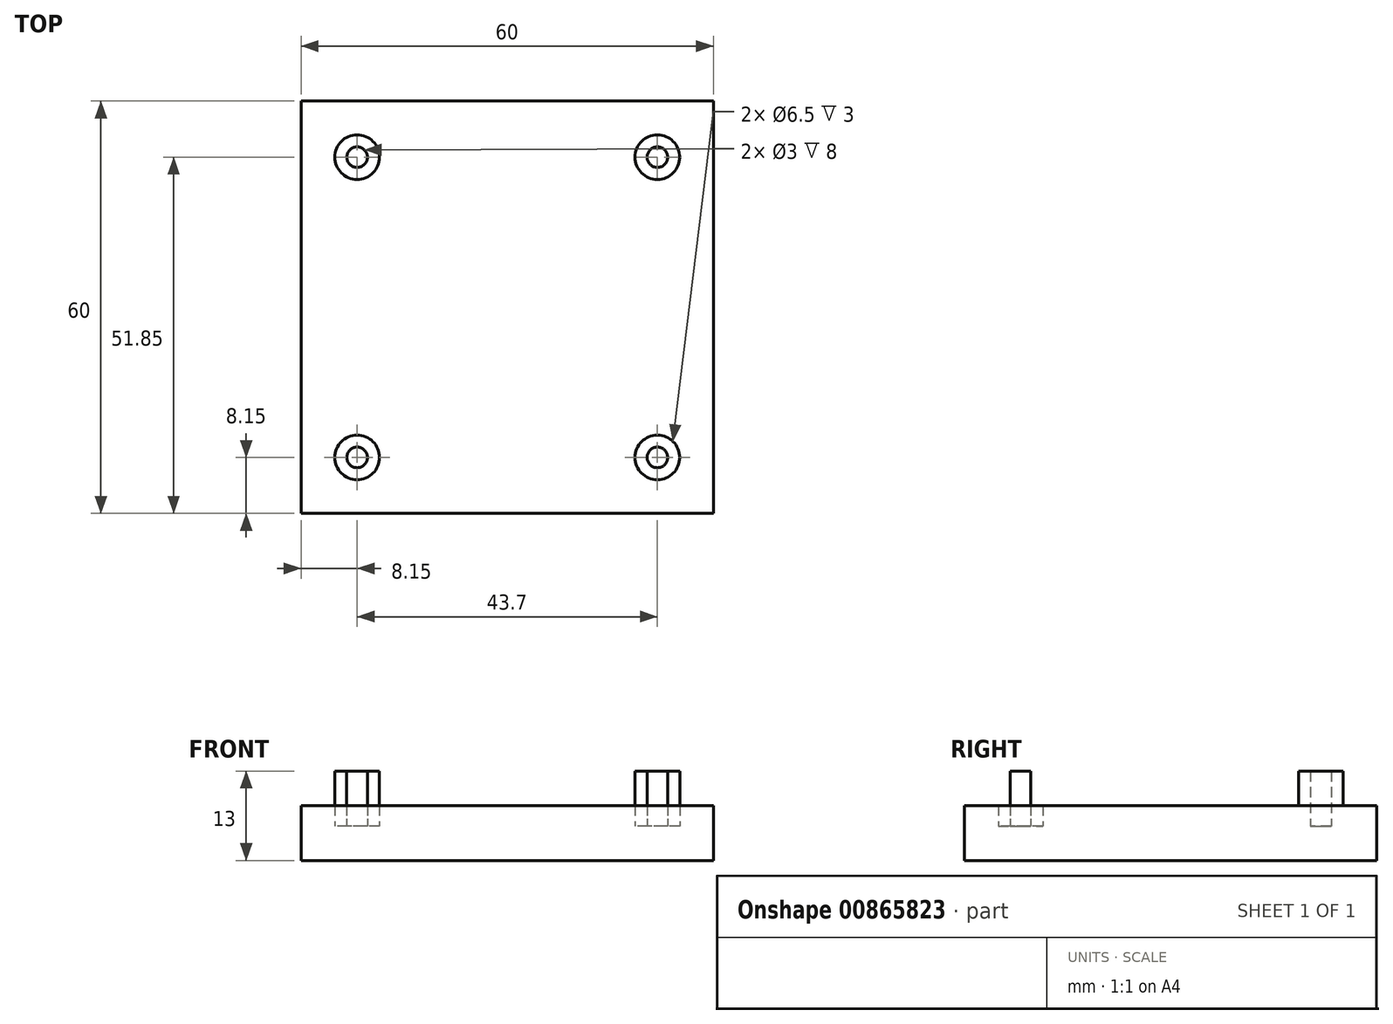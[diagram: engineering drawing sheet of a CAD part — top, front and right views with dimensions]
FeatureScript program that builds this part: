
annotation { "Feature Type Name" : "Feature", "Feature Type Description" : "" }
export const myFeature = defineFeature(function(context is Context, id is Id, definition is map)
    precondition{}
    {
        {
            var Q0;
            Q0=qCreatedBy(makeId("Top.planeOp"),FACE);
            var sketch = newSketch(context, id + "F0", { "sketchPlane" : qUnion([Q0])});
            skLineSegment(sketch, "E0.bottom", {"start": v(30, -40) * mm, "end": v(-30, -40) * mm});
            skLineSegment(sketch, "E0.top", {"start": v(30, 40) * mm, "end": v(-30, 40) * mm});
            skLineSegment(sketch, "E0.left", {"start": v(30, -40) * mm, "end": v(30, 40) * mm});
            skLineSegment(sketch, "E0.right", {"start": v(-30, -40) * mm, "end": v(-30, 40) * mm});
            skPoint(sketch, "E0.middle", {"position": v(0, 0) * mm});
            skLineSegment(sketch, "E1.bottom", {"start": v(30, -30) * mm, "end": v(-30, -30) * mm});
            skLineSegment(sketch, "E1.top", {"start": v(30, 30) * mm, "end": v(-30, 30) * mm});
            skLineSegment(sketch, "E1.left", {"start": v(30, -30) * mm, "end": v(30, 30) * mm});
            skLineSegment(sketch, "E1.right", {"start": v(-30, -30) * mm, "end": v(-30, 30) * mm});
            skCircle(sketch, "E2", {"center": v(-15, 35) * mm, "radius": 1.7 * mm});
            skCircle(sketch, "E3", {"center": v(15, 35) * mm, "radius": 1.7 * mm});
            skCircle(sketch, "E4.MirrorC", {"center": v(15, -35) * mm, "radius": 1.7 * mm});
            skCircle(sketch, "E5.MirrorC", {"center": v(-15, -35) * mm, "radius": 1.7 * mm});
            skCircle(sketch, "E6", {"center": v(-21.85, 21.85) * mm, "radius": 1.5 * mm});
            skCircle(sketch, "E7", {"center": v(21.85, 21.85) * mm, "radius": 1.5 * mm});
            skCircle(sketch, "E8.MirrorC", {"center": v(-21.85, -21.85) * mm, "radius": 1.5 * mm});
            skCircle(sketch, "E9.MirrorC", {"center": v(21.85, -21.85) * mm, "radius": 1.5 * mm});
            skCircle(sketch, "E10", {"center": v(-21.85, 21.85) * mm, "radius": 3.25 * mm});
            skCircle(sketch, "E11", {"center": v(21.85, 21.85) * mm, "radius": 3.25 * mm});
            skCircle(sketch, "E12.MirrorC", {"center": v(21.85, -21.85) * mm, "radius": 3.25 * mm});
            skCircle(sketch, "E13.MirrorC", {"center": v(-21.85, -21.85) * mm, "radius": 3.25 * mm});
            skSolve(sketch);
        }
        {
            var Q0;
            Q0=makeQuery(id+"F0.imprint","IMPRINT",FACE,{"disambiguationData":[TD([[makeQuery(id+"F0.imprint","IMPRINT",EDGE,{"derivedFrom":sQuery(id+"F0.wireOp",EDGE,"E1.bottom")}),-1.0]])]});
            extrude(context, id + "F1", {"entities" : qUnion([Q0]), "depth" : 8 * mm, "offsetDistance" : 25.4 * mm});
        }
        {
            var Q0;
            Q0=makeQuery(id+"F0.imprint","IMPRINT",FACE,{"disambiguationData":[TD([[makeQuery(id+"F0.imprint","IMPRINT",EDGE,{"derivedFrom":sQuery(id+"F0.wireOp",EDGE,"E6")}),-1.0]])]});
            var Q1;
            Q1=makeQuery(id+"F0.imprint","IMPRINT",FACE,{"disambiguationData":[TD([[makeQuery(id+"F0.imprint","IMPRINT",EDGE,{"derivedFrom":sQuery(id+"F0.wireOp",EDGE,"E7")}),-1.0]])]});
            var Q2;
            Q2=makeQuery(id+"F0.imprint","IMPRINT",FACE,{"disambiguationData":[TD([[makeQuery(id+"F0.imprint","IMPRINT",EDGE,{"derivedFrom":sQuery(id+"F0.wireOp",EDGE,"E8.MirrorC")}),1.0]])]});
            var Q3;
            Q3=makeQuery(id+"F0.imprint","IMPRINT",FACE,{"disambiguationData":[TD([[makeQuery(id+"F0.imprint","IMPRINT",EDGE,{"derivedFrom":sQuery(id+"F0.wireOp",EDGE,"E9.MirrorC")}),1.0]])]});
            extrude(context, id + "F2", {"entities" : qUnion([Q0, Q1, Q2, Q3]), "operationType" : NewBodyOperationType.ADD, "depth" : 13 * mm, "offsetDistance" : 25.4 * mm});
        }
        {
            var Q0;
            Q0=makeQuery(id+"F0.imprint","IMPRINT",FACE,{"disambiguationData":[TD([[makeQuery(id+"F0.imprint","IMPRINT",EDGE,{"derivedFrom":sQuery(id+"F0.wireOp",EDGE,"E6")}),1.0]])]});
            var Q1;
            Q1=makeQuery(id+"F0.imprint","IMPRINT",FACE,{"disambiguationData":[TD([[makeQuery(id+"F0.imprint","IMPRINT",EDGE,{"derivedFrom":sQuery(id+"F0.wireOp",EDGE,"E7")}),1.0]])]});
            var Q2;
            Q2=makeQuery(id+"F0.imprint","IMPRINT",FACE,{"disambiguationData":[TD([[makeQuery(id+"F0.imprint","IMPRINT",EDGE,{"derivedFrom":sQuery(id+"F0.wireOp",EDGE,"E8.MirrorC")}),-1.0]])]});
            var Q3;
            Q3=makeQuery(id+"F0.imprint","IMPRINT",FACE,{"disambiguationData":[TD([[makeQuery(id+"F0.imprint","IMPRINT",EDGE,{"derivedFrom":sQuery(id+"F0.wireOp",EDGE,"E9.MirrorC")}),-1.0]])]});
            extrude(context, id + "F3", {"entities" : qUnion([Q0, Q1, Q2, Q3]), "operationType" : NewBodyOperationType.ADD, "depth" : 5 * mm, "offsetDistance" : 25.4 * mm});
        }
    });
